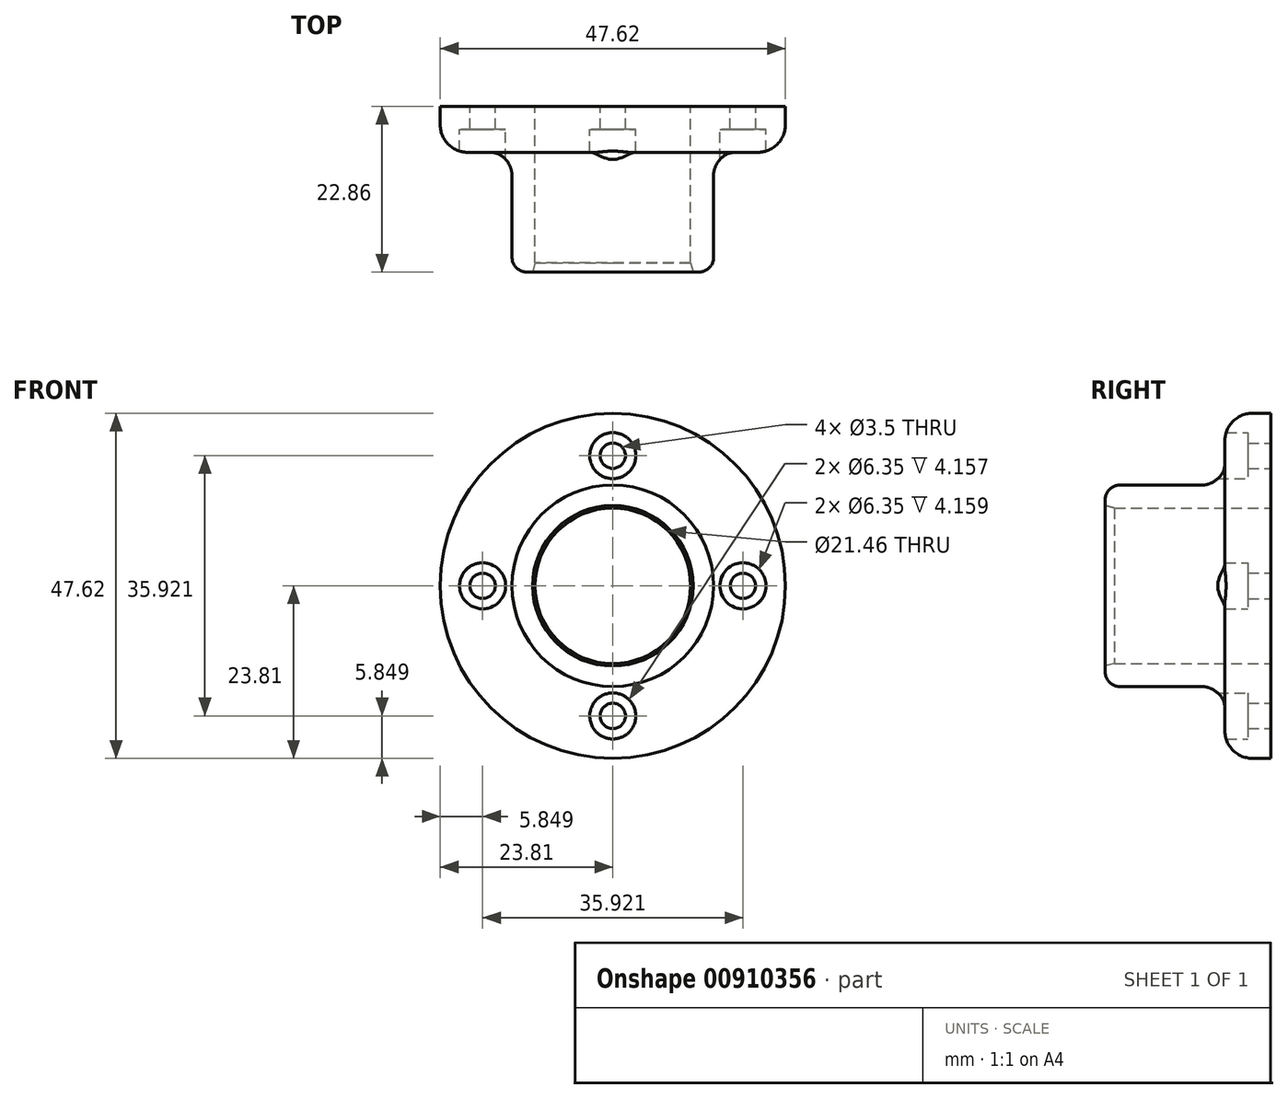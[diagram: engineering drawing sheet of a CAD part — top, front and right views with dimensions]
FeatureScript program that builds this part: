
annotation { "Feature Type Name" : "Feature", "Feature Type Description" : "" }
export const myFeature = defineFeature(function(context is Context, id is Id, definition is map)
    precondition{}
    {
        {
            var Q0;
            Q0=qCreatedBy(makeId("Right.planeOp"),FACE);
            var sketch = newSketch(context, id + "F0", { "sketchPlane" : qUnion([Q0])});
            skLineSegment(sketch, "E0", {"start": v(-21.6, 10.73) * mm, "end": v(0, 10.73) * mm});
            skLineSegment(sketch, "E1", {"start": v(0, 10.73) * mm, "end": v(0, 23.81) * mm});
            skLineSegment(sketch, "E2", {"start": v(0, 23.81) * mm, "end": v(-6.35, 23.81) * mm});
            skLineSegment(sketch, "E3", {"start": v(-6.35, 23.81) * mm, "end": v(-6.35, 17.08) * mm});
            skLineSegment(sketch, "E4", {"start": v(-9.52, 13.9) * mm, "end": v(-22.86, 13.9) * mm});
            skLineSegment(sketch, "E5", {"start": v(-22.86, 13.9) * mm, "end": v(-22.86, 11.07) * mm});
            skArc(sketch, "E6", {"start": v(-9.52, 13.9) * mm, "mid": v(-7.28, 14.84) * mm, "end": v(-6.35, 17.08) * mm});
            skLineSegment(sketch, "E7", {"start": v(-22.86, 11.07) * mm, "end": v(-21.6, 10.73) * mm});
            skLineSegment(sketch, "E8", {"start": v(0, 0) * mm, "end": v(-22.86, 0) * mm, "construction": true});
            skSolve(sketch);
        }
        {
            var Q0;
            Q0 = qSketchRegion(id + "F0", true);
            var Q1;
            Q1=sQuery(id+"F0.wireOp",EDGE,"E8");
            revolve(context, id + "F1", {"surfaceOperationType" : NewSurfaceOperationType.NEW, "entities" : qUnion([Q0]), "axis" : qUnion([Q1]), "revolveType" : RevolveType.FULL});
        }
        {
            var Q0;
            Q0=makeQuery(id+"F1.opRevolve","SWEPT_EDGE",EDGE,{"disambiguationData":[OSD([sQuery(id+"F0.wireOp",EDGE,"E4"),sQuery(id+"F0.wireOp",EDGE,"E5")])]});
            fillet(context, id + "F2", {"entities" : qUnion([Q0]), "radius" : 2.03 * mm, "tangentPropagation" : true, "allowEdgeOverflow" : false});
        }
        {
            var Q0;
            Q0=makeQuery(id+"F1.opRevolve","SWEPT_FACE",FACE,{"disambiguationData":[OSD([sQuery(id+"F0.wireOp",EDGE,"E5")])]});
            var sketch = newSketch(context, id + "F3", { "sketchPlane" : qUnion([Q0])});
            skPoint(sketch, "E9", {"position": v(17.96, 0) * mm});
            skPoint(sketch, "E10", {"position": v(0, -17.96) * mm});
            skPoint(sketch, "E11", {"position": v(-17.96, 0) * mm});
            skPoint(sketch, "E12", {"position": v(0, 17.96) * mm});
            skLineSegment(sketch, "E13", {"start": v(-17.96, 0) * mm, "end": v(0, -17.96) * mm});
            skLineSegment(sketch, "E14", {"start": v(17.96, 0) * mm, "end": v(0, 17.96) * mm});
            skLineSegment(sketch, "E15", {"start": v(-17.96, 0) * mm, "end": v(0, 17.96) * mm});
            skLineSegment(sketch, "E16", {"start": v(17.96, 0) * mm, "end": v(0, -17.96) * mm});
            skSolve(sketch);
        }
        {
            var Q0;
            Q0=sQuery(id+"F3.wireOp",VERTEX,"E11");
            var Q1;
            Q1=sQuery(id+"F3.wireOp",VERTEX,"E12");
            var Q2;
            Q2=sQuery(id+"F3.wireOp",VERTEX,"E9");
            var Q3;
            Q3=sQuery(id+"F3.wireOp",VERTEX,"E10");
            var Q4;
            Q4=makeQuery(id+"F1.opRevolve","SWEPT_BODY",BODY,{"disambiguationData":[OSD([sQuery(id+"F0.wireOp",EDGE,"E0"),sQuery(id+"F0.wireOp",EDGE,"E1"),sQuery(id+"F0.wireOp",EDGE,"E2"),sQuery(id+"F0.wireOp",EDGE,"E3"),sQuery(id+"F0.wireOp",EDGE,"E4"),sQuery(id+"F0.wireOp",EDGE,"E5"),sQuery(id+"F0.wireOp",EDGE,"E6"),sQuery(id+"F0.wireOp",EDGE,"E7")])]});
            hole(context, id + "F4", {"style" : HoleStyle.C_BORE, "endStyle" : HoleEndStyle.THROUGH, "holeDiameter" : 3.5 * mm, "cBoreDiameter" : 6.35 * mm, "cBoreDepth" : 19.68 * mm, "majorDiameter" : 6.35 * mm, "isTappedThrough" : true, "tappedDepth" : 12.7 * mm, "tapClearance" : 3, "startFromSketch" : true, "locations" : qUnion([Q0, Q1, Q2, Q3]), "scope" : qUnion([Q4])});
        }
        {
            var Q0;
            Q0=makeQuery(id+"F1.opRevolve","SWEPT_EDGE",EDGE,{"disambiguationData":[OSD([sQuery(id+"F0.wireOp",EDGE,"E2"),sQuery(id+"F0.wireOp",EDGE,"E3")])]});
            fillet(context, id + "F5", {"entities" : qUnion([Q0]), "radius" : 3.8 * mm, "tangentPropagation" : true, "allowEdgeOverflow" : false});
        }
    });
